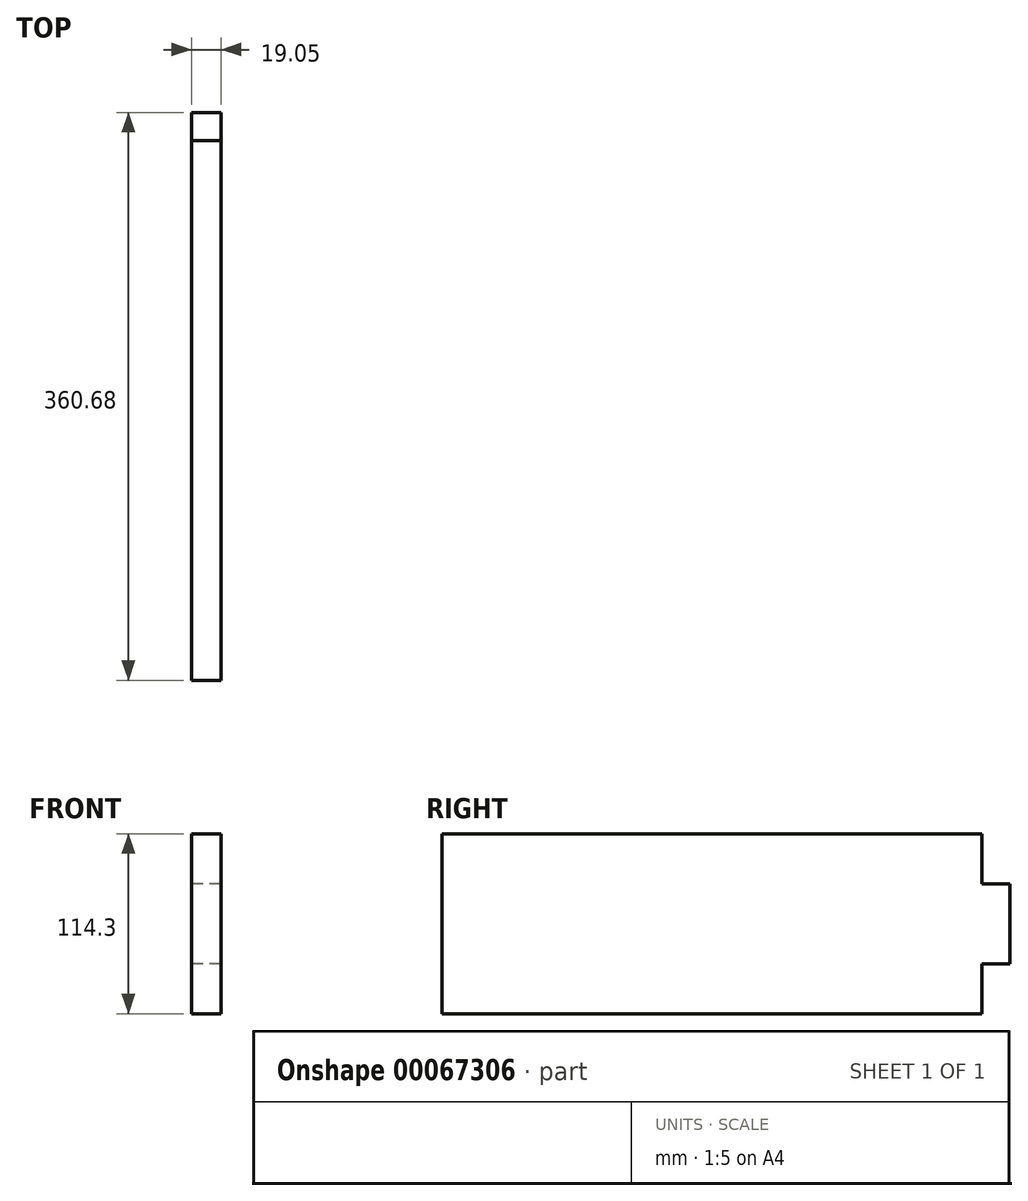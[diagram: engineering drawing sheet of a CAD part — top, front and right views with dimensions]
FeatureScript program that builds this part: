
annotation { "Feature Type Name" : "Feature", "Feature Type Description" : "" }
export const myFeature = defineFeature(function(context is Context, id is Id, definition is map)
    precondition{}
    {
        {
            var Q0;
            Q0=qCreatedBy(makeId("Right.planeOp"),FACE);
            var sketch = newSketch(context, id + "F0", { "sketchPlane" : qUnion([Q0])});
            skLineSegment(sketch, "E0.bottom", {"start": v(-171.45, 0) * mm, "end": v(171.45, 0) * mm});
            skLineSegment(sketch, "E0.top", {"start": v(-171.45, -114.3) * mm, "end": v(171.45, -114.3) * mm});
            skLineSegment(sketch, "E0.left", {"start": v(-171.45, 0) * mm, "end": v(-171.45, -114.3) * mm});
            skLineSegment(sketch, "E0.right", {"start": v(171.45, 0) * mm, "end": v(171.45, -114.3) * mm});
            skLineSegment(sketch, "E1.bottom", {"start": v(-69.85, -114.3) * mm, "end": v(82.55, -114.3) * mm});
            skLineSegment(sketch, "E1.top", {"start": v(-69.85, -132.08) * mm, "end": v(82.55, -132.08) * mm});
            skLineSegment(sketch, "E1.left", {"start": v(-69.85, -114.3) * mm, "end": v(-69.85, -132.08) * mm});
            skLineSegment(sketch, "E1.right", {"start": v(82.55, -114.3) * mm, "end": v(82.55, -132.08) * mm});
            skLineSegment(sketch, "E2.bottom", {"start": v(171.45, -31.75) * mm, "end": v(189.23, -31.75) * mm});
            skLineSegment(sketch, "E2.top", {"start": v(171.45, -82.55) * mm, "end": v(189.23, -82.55) * mm});
            skLineSegment(sketch, "E2.left", {"start": v(171.45, -31.75) * mm, "end": v(171.45, -82.55) * mm});
            skLineSegment(sketch, "E2.right", {"start": v(189.23, -31.75) * mm, "end": v(189.23, -82.55) * mm});
            skLineSegment(sketch, "E3", {"start": v(82.55, -114.3) * mm, "end": v(171.45, -114.3) * mm});
            skSolve(sketch);
        }
        {
            var Q0;
            {var subQ4=sQuery(id+"F0.wireOp",EDGE,"E0.left");Q0=makeQuery(id+"F0.imprint","IMPRINT",FACE,{"disambiguationData":[TD([[makeQuery(id+"F0.imprint","IMPRINT",EDGE,{"derivedFrom":subQ4}),1.0]])]});}
            var Q1;
            Q1=makeQuery(id+"F0.imprint","IMPRINT",FACE,{"disambiguationData":[TD([[makeQuery(id+"F0.imprint","IMPRINT",EDGE,{"derivedFrom":sQuery(id+"F0.wireOp",EDGE,"2062a582-d9c8-4e96-ad8d-9322998dc825.bottom")}),1.0]])]});
            var Q2;
            Q2=makeQuery(id+"F0.imprint","IMPRINT",FACE,{"disambiguationData":[TD([[makeQuery(id+"F0.imprint","IMPRINT",EDGE,{"derivedFrom":sQuery(id+"F0.wireOp",EDGE,"E1.bottom")}),-1.0]])]});
            var Q3;
            Q3=makeQuery(id+"F0.imprint","IMPRINT",FACE,{"disambiguationData":[TD([[makeQuery(id+"F0.imprint","IMPRINT",EDGE,{"derivedFrom":sQuery(id+"F0.wireOp",EDGE,"E2.bottom")}),-1.0]])]});
            extrude(context, id + "F1", {"entities" : qUnion([Q0, Q1, Q2, Q3]), "depth" : 19.05 * mm});
        }
    });
